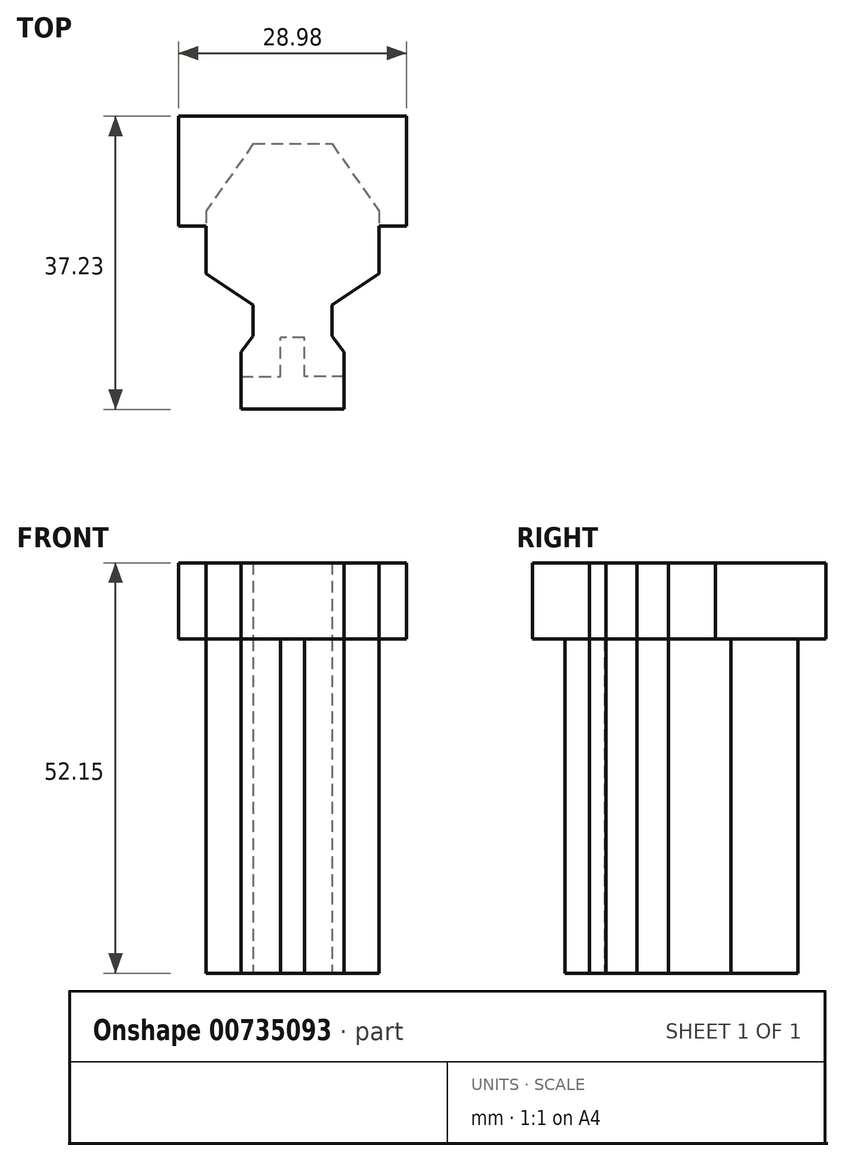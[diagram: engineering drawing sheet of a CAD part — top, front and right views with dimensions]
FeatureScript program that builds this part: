
annotation { "Feature Type Name" : "Feature", "Feature Type Description" : "" }
export const myFeature = defineFeature(function(context is Context, id is Id, definition is map)
    precondition{}
    {
        {
            var Q0;
            Q0=qCreatedBy(makeId("Top.planeOp"),FACE);
            var sketch = newSketch(context, id + "F0", { "sketchPlane" : qUnion([Q0])});
            skLineSegment(sketch, "E0", {"start": v(0, 0) * mm, "end": v(5, 0) * mm});
            skLineSegment(sketch, "E1", {"start": v(5, 0) * mm, "end": v(11, -8.56) * mm});
            skLineSegment(sketch, "E2", {"start": v(11, -8.56) * mm, "end": v(11, -16.48) * mm});
            skLineSegment(sketch, "E3", {"start": v(11, -16.48) * mm, "end": v(5, -20.5) * mm});
            skLineSegment(sketch, "E4", {"start": v(5, -20.5) * mm, "end": v(5, -24.4) * mm});
            skLineSegment(sketch, "E5", {"start": v(5, -24.4) * mm, "end": v(6.53, -26.49) * mm});
            skLineSegment(sketch, "E6", {"start": v(6.53, -29.6) * mm, "end": v(1.5, -29.6) * mm});
            skLineSegment(sketch, "E7", {"start": v(0, 0) * mm, "end": v(0, -24.6) * mm});
            skLineSegment(sketch, "E8", {"start": v(1.5, -29.6) * mm, "end": v(1.5, -24.6) * mm});
            skLineSegment(sketch, "E9", {"start": v(1.5, -24.6) * mm, "end": v(0, -24.6) * mm});
            skPoint(sketch, "E10.orphan", {"position": v(0, -29.6) * mm});
            skLineSegment(sketch, "E11", {"start": v(6.53, -29.6) * mm, "end": v(6.53, -26.49) * mm});
            skSolve(sketch);
        }
        {
            var Q0;
            Q0=makeQuery(id+"F0.imprint","IMPRINT",FACE,{"disambiguationData":[TD([[makeQuery(id+"F0.imprint","IMPRINT",EDGE,{"derivedFrom":sQuery(id+"F0.wireOp",EDGE,"E0")}),-1.0]])]});
            extrude(context, id + "F1", {"entities" : qUnion([Q0]), "depth" : 42.45 * mm, "offsetDistance" : 25 * mm});
        }
        {
            var Q0;
            Q0=makeQuery(id+"F1.opExtrude","SWEPT_BODY",BODY,{"disambiguationData":[OSD([sQuery(id+"F0.wireOp",EDGE,"E0"),sQuery(id+"F0.wireOp",EDGE,"E1"),sQuery(id+"F0.wireOp",EDGE,"E2"),sQuery(id+"F0.wireOp",EDGE,"E3"),sQuery(id+"F0.wireOp",EDGE,"E4"),sQuery(id+"F0.wireOp",EDGE,"E5"),sQuery(id+"F0.wireOp",EDGE,"E6"),sQuery(id+"F0.wireOp",EDGE,"E7")])]});
            var Q1;
            Q1=makeQuery(id+"F1.opExtrude","SWEPT_FACE",FACE,{"disambiguationData":[OSD([sQuery(id+"F0.wireOp",EDGE,"E7")])]});
            mirror(context, id + "F2", {"operationType" : NewBodyOperationType.ADD, "entities" : qUnion([Q0]), "mirrorPlane" : qUnion([Q1])});
        }
        {
            var Q0;
            {var subQ0=makeQuery(id+"F1.opExtrude","CAP_FACE",FACE,{"disambiguationData":[OSD([sQuery(id+"F0.wireOp",EDGE,"E0"),sQuery(id+"F0.wireOp",EDGE,"E1"),sQuery(id+"F0.wireOp",EDGE,"E2"),sQuery(id+"F0.wireOp",EDGE,"E3"),sQuery(id+"F0.wireOp",EDGE,"E4"),sQuery(id+"F0.wireOp",EDGE,"E5"),sQuery(id+"F0.wireOp",EDGE,"E6"),sQuery(id+"F0.wireOp",EDGE,"E7"),sQuery(id+"F0.wireOp",EDGE,"E8"),sQuery(id+"F0.wireOp",EDGE,"E9")])],"isStart":false});Q0=makeQuery(id+"F2.boolean.opBoolean","MERGE",FACE,{"derivedFrom":[subQ0,makeQuery(id+"F2.opPattern","COPY",FACE,{"derivedFrom":subQ0,"instanceName":"1"})]});}
            var sketch = newSketch(context, id + "F3", { "sketchPlane" : qUnion([Q0])});
            skLineSegment(sketch, "E12", {"start": v(14.5, -10.48) * mm, "end": v(14.5, 3.5) * mm});
            skLineSegment(sketch, "E13", {"start": v(14.5, 3.5) * mm, "end": v(-14.5, 3.5) * mm});
            skLineSegment(sketch, "E14", {"start": v(-14.5, 3.5) * mm, "end": v(-14.5, -10.48) * mm});
            skLineSegment(sketch, "E15", {"start": v(11, -16.48) * mm, "end": v(-11, -16.48) * mm});
            skLineSegment(sketch, "E16", {"start": v(11, -16.48) * mm, "end": v(5, -20.5) * mm});
            skLineSegment(sketch, "E17", {"start": v(5, -20.5) * mm, "end": v(5, -24.4) * mm});
            skLineSegment(sketch, "E18", {"start": v(5, -24.4) * mm, "end": v(6.37, -26.27) * mm});
            skLineSegment(sketch, "E19", {"start": v(-11, -16.48) * mm, "end": v(-5, -20.5) * mm});
            skLineSegment(sketch, "E20", {"start": v(-5, -20.5) * mm, "end": v(-5, -24.4) * mm});
            skLineSegment(sketch, "E21", {"start": v(-6.53, -26.49) * mm, "end": v(-6.53, -33.73) * mm});
            skLineSegment(sketch, "E22", {"start": v(-6.53, -33.73) * mm, "end": v(6.53, -33.73) * mm});
            skLineSegment(sketch, "E23", {"start": v(6.53, -33.73) * mm, "end": v(6.53, -26.49) * mm});
            skLineSegment(sketch, "E24", {"start": v(6.53, -26.49) * mm, "end": v(-6.53, -26.49) * mm});
            skLineSegment(sketch, "E25", {"start": v(14.5, -10.48) * mm, "end": v(11, -10.48) * mm});
            skLineSegment(sketch, "E26", {"start": v(11, -10.48) * mm, "end": v(11, -16.48) * mm});
            skLineSegment(sketch, "E27", {"start": v(-11, -10.48) * mm, "end": v(-14.5, -10.48) * mm});
            skLineSegment(sketch, "E28", {"start": v(-11, -10.48) * mm, "end": v(-11, -16.48) * mm});
            skLineSegment(sketch, "E29", {"start": v(6.53, -26.49) * mm, "end": v(5, -24.4) * mm});
            skLineSegment(sketch, "E30", {"start": v(5, -20.5) * mm, "end": v(11, -16.48) * mm});
            skLineSegment(sketch, "E31", {"start": v(-6.53, -26.49) * mm, "end": v(-5, -24.4) * mm});
            skLineSegment(sketch, "E32", {"start": v(-5, -20.5) * mm, "end": v(-11, -16.48) * mm});
            skSolve(sketch);
        }
        {
            var Q0;
            Q0 = qSketchRegion(id + "F3", true);
            extrude(context, id + "F4", {"entities" : qUnion([Q0]), "depth" : 9.7 * mm, "offsetDistance" : 25 * mm});
        }
    });
